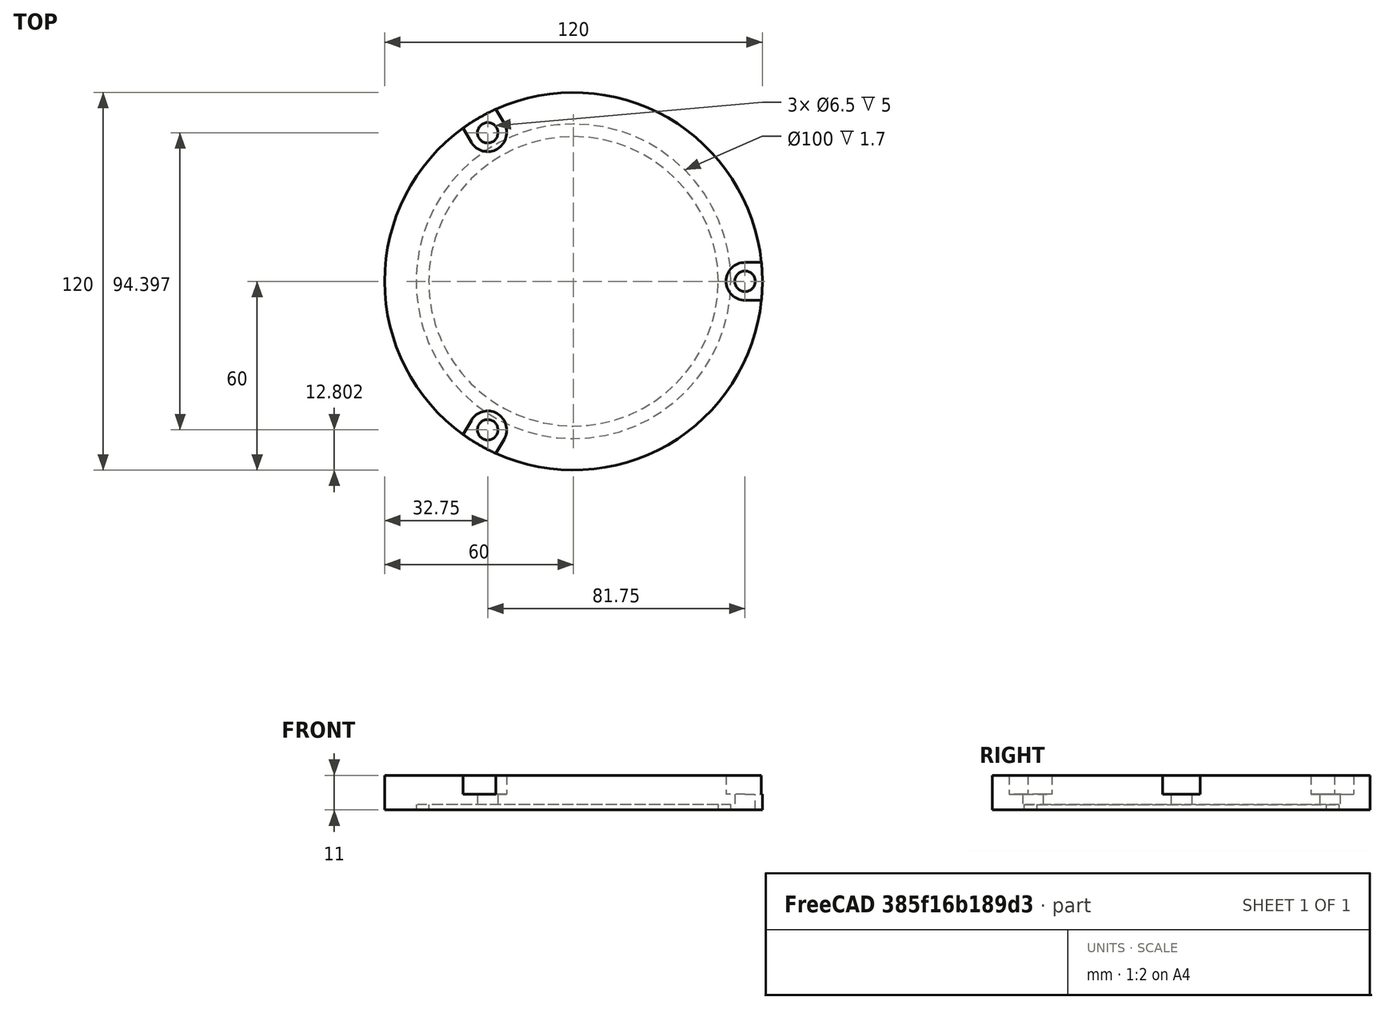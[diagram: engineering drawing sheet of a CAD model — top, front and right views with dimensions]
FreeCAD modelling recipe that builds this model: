
FCSTD DOCUMENT  (FreeCAD 0.20R29603 (Git))
Label: PhilippsXL30_Blindflange_120
License: All rights reserved
LicenseURL: http://en.wikipedia.org/wiki/All_rights_reserved
objects: TechDraw::DrawViewDimension×12, Part::Cylinder×9, Part::Cut×4, Part::Compound×4, Part::Box×3, Part::MultiFuse×3, TechDraw::DrawProjGroupItem×2, Part::Feature×1, TechDraw::DrawSVGTemplate×1, TechDraw::DrawProjGroup×1, TechDraw::DrawViewSection×1, TechDraw::DrawPage×1
note: 24 computed .brp shape members not serialized (recipe doc carries the construction recipe); baked Part::Feature solids carry a one-line shape summary decoded from their .brp

FEATURE [Part::Cylinder] Cylinder  label="Zylinder"
  Angle = 360
  AttacherType = Attacher::AttachEngine3D
  FirstAngle = 0
  Height = 11
  Radius = 60
  SecondAngle = 0
FEATURE [Part::Cylinder] Cylinder001  label="Zylinder001"
  Angle = 360
  AttacherType = Attacher::AttachEngine3D
  FirstAngle = 0
  Height = 1.7
  Radius = 50
  SecondAngle = 0
FEATURE [Part::Cylinder] Cylinder002  label="Zylinder002"
  Angle = 360
  AttacherType = Attacher::AttachEngine3D
  FirstAngle = 0
  Height = 1.7
  Radius = 46
  SecondAngle = 0
FEATURE [Part::Cut] Cut
  Base = -> Cylinder001
  Tool = -> Cylinder002
FEATURE [Part::Cut] Cut001
  Base = -> Cylinder
  Tool = -> Cut
FEATURE [Part::Cylinder] Cylinder003  label="Zylinder003"
  Angle = 360
  AttacherType = Attacher::AttachEngine3D
  FirstAngle = 0
  Height = 13
  Placement = pos=(54.5,0,0) rot=(0,0,1;0rad)
  Radius = 3.25
  SecondAngle = 0
FEATURE [Part::Cylinder] Cylinder004  label="Zylinder004"
  Angle = 360
  AttacherType = Attacher::AttachEngine3D
  FirstAngle = 0
  Height = 13
  Placement = pos=(54.5,0,0) rot=(0,0,1;0rad)
  Radius = 3.25
  SecondAngle = 0
FEATURE [Part::Cylinder] Cylinder005  label="Zylinder005"
  Angle = 360
  AttacherType = Attacher::AttachEngine3D
  FirstAngle = 0
  Height = 13
  Placement = pos=(54.5,0,0) rot=(0,0,1;0rad)
  Radius = 3.25
  SecondAngle = 0
FEATURE [Part::Compound] Compound
  Links = -> [Cylinder004]
  Placement = pos=(0,0,0) rot=(0,0,1;2.0944rad)
FEATURE [Part::Compound] Compound001
  Links = -> [Cylinder005]
  Placement = pos=(0,0,0) rot=(0,0,1;4.18879rad)
FEATURE [Part::Compound] Compound002
  Links = -> [Compound001,Cylinder003,Compound]
FEATURE [Part::Cut] Cut002
  Base = -> Cut001
  Tool = -> Compound002
FEATURE [Part::Cylinder] Cylinder006  label="Zylinder006"
  Angle = 360
  AttacherType = Attacher::AttachEngine3D
  FirstAngle = 0
  Height = 6
  Placement = pos=(54.5,0,5) rot=(0,0,1;0rad)
  Radius = 6
  SecondAngle = 0
FEATURE [Part::Box] Box  label="Würfel"
  AttacherType = Attacher::AttachEngine3D
  Height = 6
  Length = 10
  Placement = pos=(54.5,-6,5) rot=(0,0,1;0rad)
  Width = 12
FEATURE [Part::MultiFuse] Fusion
  Shapes = -> [Cylinder006,Box]
FEATURE [Part::Box] Box001  label="Würfel001"
  AttacherType = Attacher::AttachEngine3D
  Height = 6
  Length = 10
  Placement = pos=(54.5,-6,5) rot=(0,0,1;0rad)
  Width = 12
FEATURE [Part::Cylinder] Cylinder007  label="Zylinder007"
  Angle = 360
  AttacherType = Attacher::AttachEngine3D
  FirstAngle = 0
  Height = 6
  Placement = pos=(54.5,0,5) rot=(0,0,1;0rad)
  Radius = 6
  SecondAngle = 0
FEATURE [Part::MultiFuse] Fusion001
  Placement = pos=(0,0,0) rot=(0,0,1;2.0944rad)
  Shapes = -> [Cylinder007,Box001]
FEATURE [Part::Box] Box002  label="Würfel002"
  AttacherType = Attacher::AttachEngine3D
  Height = 6
  Length = 10
  Placement = pos=(54.5,-6,5) rot=(0,0,1;0rad)
  Width = 12
FEATURE [Part::Cylinder] Cylinder008  label="Zylinder008"
  Angle = 360
  AttacherType = Attacher::AttachEngine3D
  FirstAngle = 0
  Height = 6
  Placement = pos=(54.5,0,5) rot=(0,0,1;0rad)
  Radius = 6
  SecondAngle = 0
FEATURE [Part::MultiFuse] Fusion002
  Placement = pos=(0,0,0) rot=(0,0,1;4.18879rad)
  Shapes = -> [Cylinder008,Box002]
FEATURE [Part::Compound] Compound003
  Links = -> [Fusion002,Fusion,Fusion001]
FEATURE [Part::Cut] Cut003
  Base = -> Cut002
  Tool = -> Compound003
FEATURE [Part::Feature] Cut003_solid  label="PhilippsXL30_Blindlfnage_120"
  shape: bbox 120 x 120 x 11 mm, 31 faces (baked)
FEATURE [TechDraw::DrawSVGTemplate] Template
  EditableTexts = Designed_by_Name=Thomas Spielauer; FC-Date=2023-08-09; FC-SC=mm; FC-Title=120mm Blindflange; Subtitle=XL30 ESEM compatible
  Height = 210
  Orientation = 1
  Width = 297
FEATURE [TechDraw::DrawProjGroupItem] ProjItem  label="Front"
  CoarseView = false
  Direction = (0,0,1)
  Focus = 100
  HardHidden = false
  IsoCount = 0
  IsoHidden = false
  IsoVisible = false
  LockPosition = true
  Perspective = false
  Rotation = 0
  RotationVector = (-1,0,0)
  Scale = 0.5
  ScaleType = 2
  SeamHidden = false
  SeamVisible = true
  SmoothHidden = false
  SmoothVisible = true
  Source = -> [Cut003_solid]
  Type = 0
  X = 0
  XDirection = (-1,0,0)
  Y = 0
FEATURE [TechDraw::DrawProjGroupItem] ProjItem002  label="Rear"
  CoarseView = false
  Direction = (0,0,-1)
  Focus = 100
  HardHidden = false
  IsoCount = 0
  IsoHidden = false
  IsoVisible = false
  LockPosition = false
  Perspective = false
  Rotation = 0
  RotationVector = (1,0,0)
  Scale = 0.5
  ScaleType = 2
  SeamHidden = false
  SeamVisible = true
  SmoothHidden = false
  SmoothVisible = true
  Source = -> [Cut003_solid]
  Type = 3
  X = 138.137
  XDirection = (1,0,0)
  Y = 0
FEATURE [TechDraw::DrawProjGroup] ProjGroup
  Anchor = -> ProjItem
  AutoDistribute = false
  LockPosition = false
  ProjectionType = 0
  Rotation = 0
  Scale = 0.5
  ScaleType = 2
  Source = -> [Cut003_solid]
  Views = -> [ProjItem,ProjItem002]
  X = 64.0008
  Y = 154.915
  spacingX = 15
  spacingY = 15
FEATURE [TechDraw::DrawViewDimension] Dimension
  AngleOverride = false
  Arbitrary = false
  ArbitraryTolerances = false
  EqualTolerance = true
  ExtensionAngle = 0
  FormatSpec = ⌀%.2w
  FormatSpecOverTolerance = %+.2w
  FormatSpecUnderTolerance = %+.2w
  Inverted = false
  LineAngle = 0
  LockPosition = false
  MeasureType = 1
  OverTolerance = 0
  References2D = -> [ProjItem]
  Rotation = 0
  ScaleType = 0
  TheoreticalExact = false
  Type = 5
  UnderTolerance = 0
  X = 4.59028
  Y = 5.0141
FEATURE [TechDraw::DrawViewDimension] Dimension001
  AngleOverride = false
  Arbitrary = false
  ArbitraryTolerances = false
  EqualTolerance = true
  ExtensionAngle = 0
  FormatSpec = ⌀%.2w
  FormatSpecOverTolerance = %+.2w
  FormatSpecUnderTolerance = %+.2w
  Inverted = false
  LineAngle = 0
  LockPosition = false
  MeasureType = 1
  OverTolerance = 0
  References2D = -> [ProjItem002]
  Rotation = 0
  ScaleType = 0
  TheoreticalExact = false
  Type = 5
  UnderTolerance = 0
  X = 41.7003
  Y = 21.8519
FEATURE [TechDraw::DrawViewDimension] Dimension002
  AngleOverride = false
  Arbitrary = false
  ArbitraryTolerances = false
  EqualTolerance = true
  ExtensionAngle = 0
  FormatSpec = ⌀%.2w
  FormatSpecOverTolerance = %+.2w
  FormatSpecUnderTolerance = %+.2w
  Inverted = false
  LineAngle = 0
  LockPosition = false
  MeasureType = 1
  OverTolerance = 0
  References2D = -> [ProjItem002]
  Rotation = 0
  ScaleType = 0
  TheoreticalExact = false
  Type = 5
  UnderTolerance = 0
  X = 37.9024
  Y = 30.5789
FEATURE [TechDraw::DrawViewDimension] Dimension003
  AngleOverride = false
  Arbitrary = false
  ArbitraryTolerances = false
  EqualTolerance = true
  ExtensionAngle = 0
  FormatSpec = ⌀%.2w (3x)
  FormatSpecOverTolerance = %+.2w
  FormatSpecUnderTolerance = %+.2w
  Inverted = false
  LineAngle = 0
  LockPosition = false
  MeasureType = 1
  OverTolerance = 0
  References2D = -> [ProjItem002]
  Rotation = 0
  ScaleType = 0
  TheoreticalExact = false
  Type = 5
  UnderTolerance = 0
  X = 48.8137
  Y = 11.6701
FEATURE [TechDraw::DrawViewDimension] Dimension004
  AngleOverride = false
  Arbitrary = false
  ArbitraryTolerances = false
  EqualTolerance = true
  ExtensionAngle = 0
  FormatSpec = ⌀%.2w
  FormatSpecOverTolerance = %+.2w
  FormatSpecUnderTolerance = %+.2w
  Inverted = false
  LineAngle = 0
  LockPosition = false
  MeasureType = 1
  OverTolerance = 0
  References2D = -> [ProjItem002]
  Rotation = 0
  ScaleType = 0
  TheoreticalExact = false
  Type = 5
  UnderTolerance = 0
  X = -12.3113
  Y = 11.3453
FEATURE [TechDraw::DrawViewDimension] Dimension005
  AngleOverride = false
  Arbitrary = false
  ArbitraryTolerances = false
  EqualTolerance = true
  ExtensionAngle = 0
  FormatSpec = %.2w
  FormatSpecOverTolerance = %+.2w
  FormatSpecUnderTolerance = %+.2w
  Inverted = false
  LineAngle = 0
  LockPosition = false
  MeasureType = 1
  OverTolerance = 0
  References2D = -> [ProjItem002]
  Rotation = 0
  ScaleType = 0
  TheoreticalExact = false
  Type = 6
  UnderTolerance = 0
  X = -30.5077
  Y = 25.616
FEATURE [TechDraw::DrawViewDimension] Dimension006
  AngleOverride = false
  Arbitrary = false
  ArbitraryTolerances = false
  EqualTolerance = true
  ExtensionAngle = 0
  FormatSpec = R%.2w
  FormatSpecOverTolerance = %+.2w
  FormatSpecUnderTolerance = %+.2w
  Inverted = false
  LineAngle = 0
  LockPosition = false
  MeasureType = 1
  OverTolerance = 0
  References2D = -> [ProjItem]
  Rotation = 0
  ScaleType = 0
  TheoreticalExact = false
  Type = 4
  UnderTolerance = 0
  X = -17.3365
  Y = -0.720462
FEATURE [TechDraw::DrawViewSection] SectionView  label="Section  - "
  BaseView = -> ProjItem
  CoarseView = false
  CutSurfaceDisplay = 2
  Direction = (0,-1,0)
  FileGeomPattern = <path>
  FileHatchPattern = <path>
  Focus = 100
  FuseBeforeCut = false
  HardHidden = false
  HatchScale = 1
  IsoCount = 0
  IsoHidden = false
  IsoVisible = false
  LockPosition = false
  NameGeomPattern = Diamond
  Perspective = false
  Rotation = 0
  ScaleType = 2
  SeamHidden = false
  SeamVisible = true
  SectionDirection = 3
  SectionNormal = (0,-1,0)
  SectionOrigin = (0,0,5.5)
  SmoothHidden = false
  SmoothVisible = true
  Source = -> [Cut003_solid]
  X = 80.9066
  XDirection = (-1,0,0)
  Y = 92.1251
FEATURE [TechDraw::DrawViewDimension] Dimension007
  AngleOverride = false
  Arbitrary = false
  ArbitraryTolerances = false
  EqualTolerance = true
  ExtensionAngle = 0
  FormatSpec = %.2w
  FormatSpecOverTolerance = %+.2w
  FormatSpecUnderTolerance = %+.2w
  Inverted = false
  LineAngle = 0
  LockPosition = false
  MeasureType = 1
  OverTolerance = 0
  References2D = -> [SectionView]
  Rotation = 0
  ScaleType = 0
  TheoreticalExact = false
  Type = 0
  UnderTolerance = 0
  X = 81.3032
  Y = 12.2748
FEATURE [TechDraw::DrawViewDimension] Dimension008
  AngleOverride = false
  Arbitrary = false
  ArbitraryTolerances = false
  EqualTolerance = true
  ExtensionAngle = 0
  FormatSpec = %.2w
  FormatSpecOverTolerance = %+.2w
  FormatSpecUnderTolerance = %+.2w
  Inverted = false
  LineAngle = 0
  LockPosition = false
  MeasureType = 1
  OverTolerance = 0
  References2D = -> [SectionView]
  Rotation = 0
  ScaleType = 0
  TheoreticalExact = false
  Type = 0
  UnderTolerance = 0
  X = 69.5088
  Y = 10.6749
FEATURE [TechDraw::DrawViewDimension] Dimension009
  AngleOverride = false
  Arbitrary = false
  ArbitraryTolerances = false
  EqualTolerance = true
  ExtensionAngle = 0
  FormatSpec = %.2w
  FormatSpecOverTolerance = %+.2w
  FormatSpecUnderTolerance = %+.2w
  Inverted = false
  LineAngle = 0
  LockPosition = false
  MeasureType = 1
  OverTolerance = 0
  References2D = -> [SectionView]
  Rotation = 0
  ScaleType = 0
  TheoreticalExact = false
  Type = 0
  UnderTolerance = 0
  X = 38.1977
  Y = -10.7901
FEATURE [TechDraw::DrawViewDimension] Dimension010
  AngleOverride = false
  Arbitrary = false
  ArbitraryTolerances = false
  EqualTolerance = true
  ExtensionAngle = 0
  FormatSpec = %.2w
  FormatSpecOverTolerance = %+.2w
  FormatSpecUnderTolerance = %+.2w
  Inverted = false
  LineAngle = 0
  LockPosition = false
  MeasureType = 1
  OverTolerance = 0
  References2D = -> [SectionView]
  Rotation = 0
  ScaleType = 0
  TheoreticalExact = false
  Type = 0
  UnderTolerance = 0
  X = -41.165
  Y = -21.9362
FEATURE [TechDraw::DrawViewDimension] Dimension011
  AngleOverride = false
  Arbitrary = false
  ArbitraryTolerances = false
  EqualTolerance = true
  ExtensionAngle = 0
  FormatSpec = %.2w
  FormatSpecOverTolerance = %+.2w
  FormatSpecUnderTolerance = %+.2w
  Inverted = false
  LineAngle = 0
  LockPosition = false
  MeasureType = 1
  OverTolerance = 0
  References2D = -> [SectionView]
  Rotation = 0
  ScaleType = 0
  TheoreticalExact = false
  Type = 0
  UnderTolerance = 0
  X = -67.0584
  Y = 9.8017
FEATURE [TechDraw::DrawPage] Page
  KeepUpdated = true
  NextBalloonIndex = 1
  ProjectionType = 0
  Template = -> Template
  Views = -> [ProjGroup,Dimension,Dimension001,Dimension002,Dimension003,Dimension004,Dimension005,Dimension006,SectionView,Dimension007,Dimension008,Dimension009,Dimension010,Dimension011]
note: 2 file-system paths scrubbed to <path> (originals preserved in the JSON sidecar)
